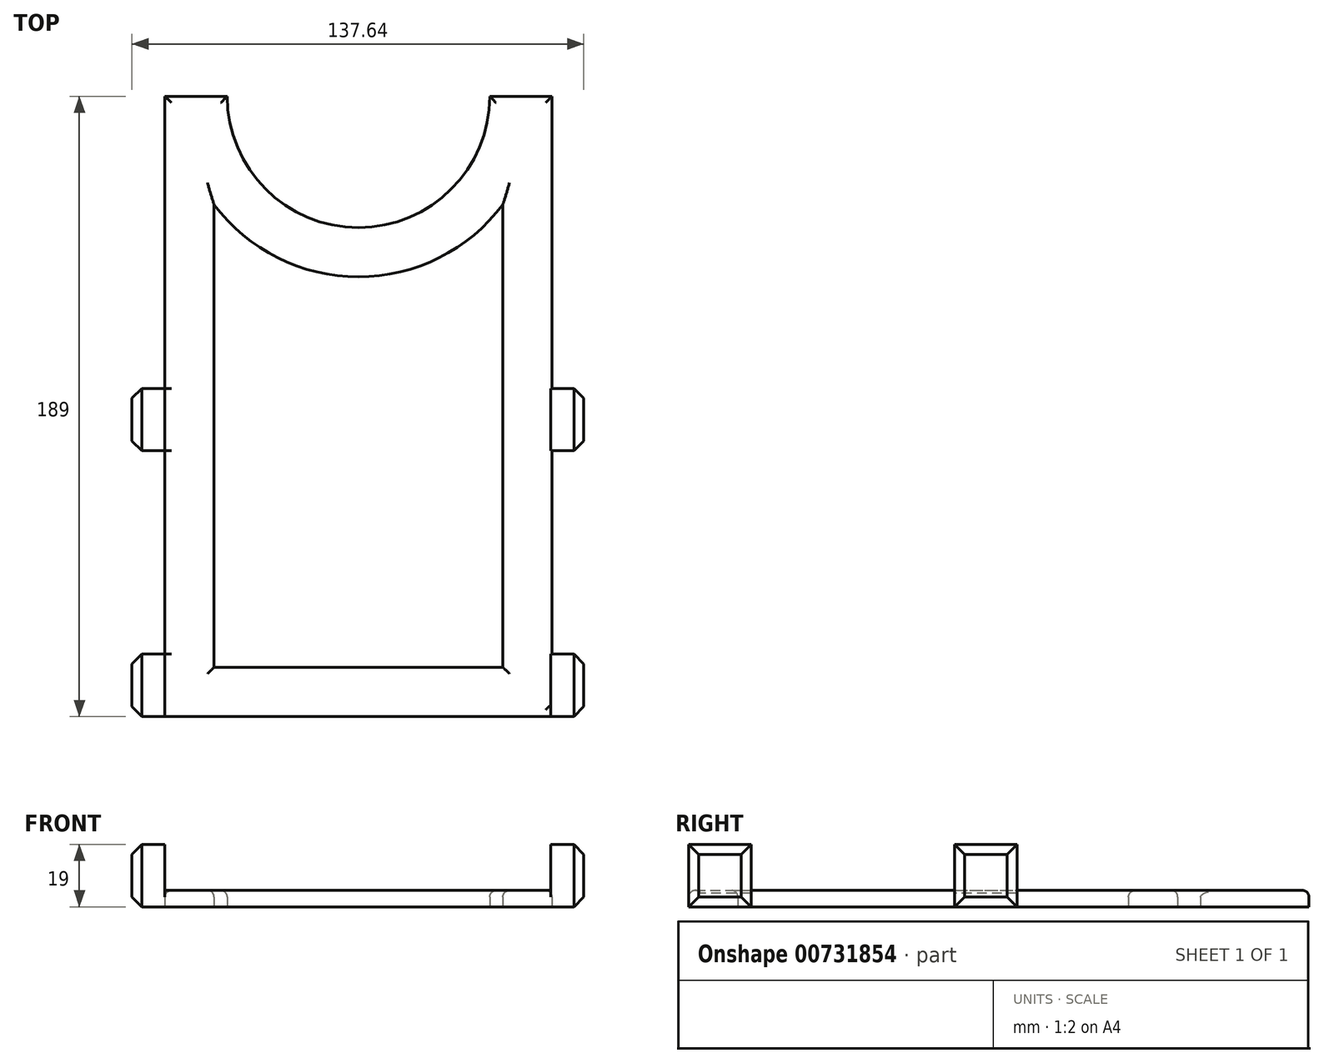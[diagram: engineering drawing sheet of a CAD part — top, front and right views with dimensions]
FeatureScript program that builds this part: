
annotation { "Feature Type Name" : "Feature", "Feature Type Description" : "" }
export const myFeature = defineFeature(function(context is Context, id is Id, definition is map)
    precondition{}
    {
        {
            var Q0;
            Q0=qCreatedBy(makeId("Top.planeOp"),FACE);
            var sketch = newSketch(context, id + "F0", { "sketchPlane" : qUnion([Q0])});
            skArc(sketch, "E0", {"start": v(-39.82, 55) * mm, "mid": v(0.18, 15) * mm, "end": v(40.18, 55) * mm});
            skLineSegment(sketch, "E1", {"start": v(-39.82, 55) * mm, "end": v(-58.82, 55) * mm});
            skLineSegment(sketch, "E2", {"start": v(-58.82, 55) * mm, "end": v(-58.82, -134) * mm});
            skLineSegment(sketch, "E3", {"start": v(-58.82, -134) * mm, "end": v(59.18, -134) * mm});
            skLineSegment(sketch, "E4", {"start": v(59.18, -134) * mm, "end": v(59.18, 55) * mm});
            skLineSegment(sketch, "E5", {"start": v(59.18, 55) * mm, "end": v(40.18, 55) * mm});
            skLineSegment(sketch, "E6.0", {"start": v(-43.82, -119) * mm, "end": v(44.18, -119) * mm});
            skLineSegment(sketch, "E6.1", {"start": v(-43.82, 22) * mm, "end": v(-43.82, -119) * mm});
            skArc(sketch, "E6.2", {"start": v(-43.82, 22) * mm, "mid": v(0.18, 0) * mm, "end": v(44.18, 22) * mm});
            skLineSegment(sketch, "E6.3", {"start": v(44.18, -119) * mm, "end": v(44.18, 22) * mm});
            skSolve(sketch);
        }
        {
            var Q0;
            Q0=qCreatedBy(makeId("Top.planeOp"),FACE);
            var sketch = newSketch(context, id + "F1", { "sketchPlane" : qUnion([Q0])});
            skLineSegment(sketch, "E7", {"start": v(-58.82, -34) * mm, "end": v(-68.82, -34) * mm});
            skLineSegment(sketch, "E8", {"start": v(-68.82, -34) * mm, "end": v(-68.82, -53) * mm});
            skLineSegment(sketch, "E9", {"start": v(-68.82, -53) * mm, "end": v(-58.82, -53) * mm});
            skLineSegment(sketch, "E10", {"start": v(-58.82, -53) * mm, "end": v(-58.82, -34) * mm});
            skLineSegment(sketch, "E11", {"start": v(-58.82, -115) * mm, "end": v(-68.82, -115) * mm});
            skLineSegment(sketch, "E12", {"start": v(-68.82, -115) * mm, "end": v(-68.82, -134) * mm});
            skLineSegment(sketch, "E13", {"start": v(-68.82, -134) * mm, "end": v(-58.82, -134) * mm});
            skLineSegment(sketch, "E14", {"start": v(-58.82, -134) * mm, "end": v(-58.82, -115) * mm});
            skLineSegment(sketch, "E15", {"start": v(-68.82, -134) * mm, "end": v(150, -134) * mm, "construction": true});
            skLineSegment(sketch, "E16.MirrorCS", {"start": v(68.82, -34) * mm, "end": v(68.82, -53) * mm});
            skLineSegment(sketch, "E17.MirrorCS", {"start": v(58.82, -34) * mm, "end": v(68.82, -34) * mm});
            skLineSegment(sketch, "E18.MirrorCS", {"start": v(58.82, -53) * mm, "end": v(58.82, -34) * mm});
            skLineSegment(sketch, "E19.MirrorCS", {"start": v(68.82, -53) * mm, "end": v(58.82, -53) * mm});
            skLineSegment(sketch, "E20.MirrorCS", {"start": v(58.82, -115) * mm, "end": v(68.82, -115) * mm});
            skLineSegment(sketch, "E21.MirrorCS", {"start": v(68.82, -115) * mm, "end": v(68.82, -134) * mm});
            skLineSegment(sketch, "E22.MirrorCS", {"start": v(58.82, -134) * mm, "end": v(58.82, -115) * mm});
            skLineSegment(sketch, "E23.MirrorCS", {"start": v(68.82, -134) * mm, "end": v(-150, -134) * mm, "construction": true});
            skLineSegment(sketch, "E24", {"start": v(58.82, -134) * mm, "end": v(68.82, -134) * mm});
            skSolve(sketch);
        }
        {
            var Q0;
            Q0=makeQuery(id+"F0.imprint","IMPRINT",FACE,{"disambiguationData":[TD([[makeQuery(id+"F0.imprint","IMPRINT",EDGE,{"derivedFrom":sQuery(id+"F0.wireOp",EDGE,"E0")}),-1.0]])]});
            extrude(context, id + "F2", {"entities" : qUnion([Q0]), "depth" : 5 * mm, "offsetDistance" : 25 * mm});
        }
        {
            var Q0;
            Q0=makeQuery(id+"F1.imprint","IMPRINT",FACE,{"disambiguationData":[TD([[makeQuery(id+"F1.imprint","IMPRINT",EDGE,{"derivedFrom":sQuery(id+"F1.wireOp",EDGE,"E16.MirrorCS")}),-1.0]])]});
            var Q1;
            Q1=makeQuery(id+"F1.imprint","IMPRINT",FACE,{"disambiguationData":[TD([[makeQuery(id+"F1.imprint","IMPRINT",EDGE,{"derivedFrom":sQuery(id+"F1.wireOp",EDGE,"E20.MirrorCS")}),-1.0]])]});
            var Q2;
            Q2=makeQuery(id+"F1.imprint","IMPRINT",FACE,{"disambiguationData":[TD([[makeQuery(id+"F1.imprint","IMPRINT",EDGE,{"derivedFrom":sQuery(id+"F1.wireOp",EDGE,"E7")}),1.0]])]});
            var Q3;
            Q3=makeQuery(id+"F1.imprint","IMPRINT",FACE,{"disambiguationData":[TD([[makeQuery(id+"F1.imprint","IMPRINT",EDGE,{"derivedFrom":sQuery(id+"F1.wireOp",EDGE,"E11")}),1.0]])]});
            extrude(context, id + "F3", {"entities" : qUnion([Q0, Q1, Q2, Q3]), "operationType" : NewBodyOperationType.ADD, "depth" : 19 * mm, "offsetDistance" : 25 * mm});
        }
        {
            var Q0;
            Q0=makeQuery(id+"F2.opExtrude","CAP_EDGE",EDGE,{"disambiguationData":[OSD([sQuery(id+"F0.wireOp",EDGE,"E3")])],"isStart":false});
            var Q1;
            {var subQ0=sQuery(id+"F0.wireOp",EDGE,"E2");var subQ1=makeQuery(id+"F2.opExtrude","SWEPT_FACE",FACE,{"disambiguationData":[OSD([subQ0])]});var subQ2=makeQuery(id+"F2.opExtrude","CAP_FACE",FACE,{"disambiguationData":[OSD([sQuery(id+"F0.wireOp",EDGE,"E0"),sQuery(id+"F0.wireOp",EDGE,"E1"),subQ0,sQuery(id+"F0.wireOp",EDGE,"E3"),sQuery(id+"F0.wireOp",EDGE,"E4"),sQuery(id+"F0.wireOp",EDGE,"E5"),sQuery(id+"F0.wireOp",EDGE,"E6.0"),sQuery(id+"F0.wireOp",EDGE,"E6.1"),sQuery(id+"F0.wireOp",EDGE,"E6.2"),sQuery(id+"F0.wireOp",EDGE,"E6.3")])],"isStart":false});Q1=makeQuery(id+"F3.boolean.opBoolean","SPLIT",EDGE,{"disambiguationData":[topologyDisambiguationEdgeConnected([subQ2,subQ1]),TD([makeQuery(id+"F3.opExtrude","SWEPT_FACE",FACE,{"disambiguationData":[OSD([sQuery(id+"F1.wireOp",EDGE,"E9")])]})])],"derivedFrom":makeQuery(id+"F2.opExtrude","CAP_EDGE",EDGE,{"disambiguationData":[OSD([subQ0])],"isStart":false})});}
            var Q2;
            {var subQ0=sQuery(id+"F0.wireOp",EDGE,"E2");var subQ1=makeQuery(id+"F2.opExtrude","SWEPT_FACE",FACE,{"disambiguationData":[OSD([subQ0])]});var subQ2=sQuery(id+"F0.wireOp",EDGE,"E1");var subQ3=makeQuery(id+"F2.opExtrude","CAP_FACE",FACE,{"disambiguationData":[OSD([sQuery(id+"F0.wireOp",EDGE,"E0"),subQ2,subQ0,sQuery(id+"F0.wireOp",EDGE,"E3"),sQuery(id+"F0.wireOp",EDGE,"E4"),sQuery(id+"F0.wireOp",EDGE,"E5"),sQuery(id+"F0.wireOp",EDGE,"E6.0"),sQuery(id+"F0.wireOp",EDGE,"E6.1"),sQuery(id+"F0.wireOp",EDGE,"E6.2"),sQuery(id+"F0.wireOp",EDGE,"E6.3")])],"isStart":false});Q2=makeQuery(id+"F3.boolean.opBoolean","SPLIT",EDGE,{"disambiguationData":[topologyDisambiguationEdgeConnected([subQ3,subQ1]),TD([makeQuery(id+"F2.opExtrude","SWEPT_FACE",FACE,{"disambiguationData":[OSD([subQ2])]})])],"derivedFrom":makeQuery(id+"F2.opExtrude","CAP_EDGE",EDGE,{"disambiguationData":[OSD([subQ0])],"isStart":false})});}
            var Q3;
            Q3=makeQuery(id+"F2.opExtrude","CAP_EDGE",EDGE,{"disambiguationData":[OSD([sQuery(id+"F0.wireOp",EDGE,"E0")])],"isStart":false});
            var Q4;
            Q4=makeQuery(id+"F2.opExtrude","CAP_EDGE",EDGE,{"disambiguationData":[OSD([sQuery(id+"F0.wireOp",EDGE,"E5")])],"isStart":false});
            var Q5;
            Q5=makeQuery(id+"F2.opExtrude","CAP_EDGE",EDGE,{"disambiguationData":[OSD([sQuery(id+"F0.wireOp",EDGE,"E1")])],"isStart":false});
            fillet(context, id + "F4", {"entities" : qUnion([Q0, Q1, Q2, Q3, Q4, Q5]), "radius" : 2 * mm, "tangentPropagation" : true, "allowEdgeOverflow" : false});
        }
        {
            var Q0;
            {var subQ0=sQuery(id+"F0.wireOp",EDGE,"E4");Q0=makeQuery(id+"F3.boolean.opBoolean","SPLIT",EDGE,{"disambiguationData":[TD([makeQuery(id+"F3.opExtrude","SWEPT_FACE",FACE,{"disambiguationData":[OSD([sQuery(id+"F1.wireOp",EDGE,"E19.MirrorCS")])]})])],"derivedFrom":makeQuery(id+"F2.opExtrude","CAP_EDGE",EDGE,{"disambiguationData":[OSD([subQ0])],"isStart":false})});}
            var Q1;
            Q1=makeQuery(id+"F2.opExtrude","CAP_EDGE",EDGE,{"disambiguationData":[OSD([sQuery(id+"F0.wireOp",EDGE,"E6.2")])],"isStart":false});
            var Q2;
            Q2=makeQuery(id+"F2.opExtrude","CAP_EDGE",EDGE,{"disambiguationData":[OSD([sQuery(id+"F0.wireOp",EDGE,"E6.1")])],"isStart":false});
            var Q3;
            Q3=makeQuery(id+"F2.opExtrude","CAP_EDGE",EDGE,{"disambiguationData":[OSD([sQuery(id+"F0.wireOp",EDGE,"E6.3")])],"isStart":false});
            var Q4;
            Q4=makeQuery(id+"F2.opExtrude","CAP_EDGE",EDGE,{"disambiguationData":[OSD([sQuery(id+"F0.wireOp",EDGE,"E6.0")])],"isStart":false});
            fillet(context, id + "F5", {"entities" : qUnion([Q0, Q1, Q2, Q3, Q4]), "radius" : 2 * mm, "tangentPropagation" : true, "allowEdgeOverflow" : false});
        }
        {
            var Q0;
            Q0=makeQuery(id+"F3.opExtrude","SWEPT_FACE",FACE,{"disambiguationData":[OSD([sQuery(id+"F1.wireOp",EDGE,"E21.MirrorCS")])]});
            var Q1;
            Q1=makeQuery(id+"F3.opExtrude","SWEPT_FACE",FACE,{"disambiguationData":[OSD([sQuery(id+"F1.wireOp",EDGE,"E16.MirrorCS")])]});
            var Q2;
            Q2=makeQuery(id+"F3.opExtrude","SWEPT_FACE",FACE,{"disambiguationData":[OSD([sQuery(id+"F1.wireOp",EDGE,"E12")])]});
            var Q3;
            Q3=makeQuery(id+"F3.opExtrude","SWEPT_FACE",FACE,{"disambiguationData":[OSD([sQuery(id+"F1.wireOp",EDGE,"E8")])]});
            chamfer(context, id + "F6", {"entities" : qUnion([Q0, Q1, Q2, Q3]), "width" : 3 * mm, "tangentPropagation" : true});
        }
    });
